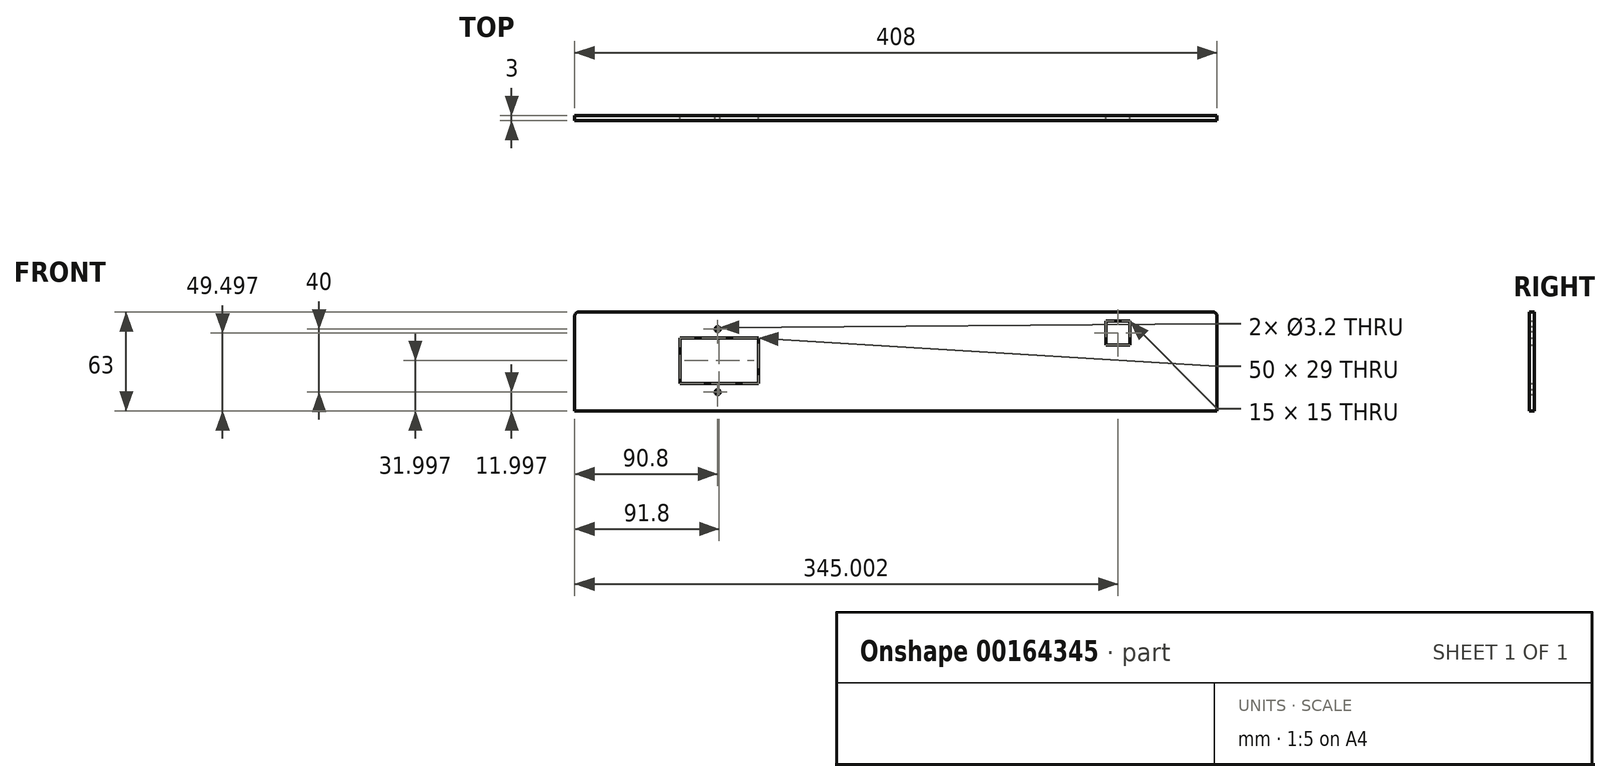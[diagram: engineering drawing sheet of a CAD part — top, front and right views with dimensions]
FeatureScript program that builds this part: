
annotation { "Feature Type Name" : "Feature", "Feature Type Description" : "" }
export const myFeature = defineFeature(function(context is Context, id is Id, definition is map)
    precondition{}
    {
        {
            var Q0;
            Q0=qCreatedBy(makeId("Front.planeOp"),FACE);
            var sketch = newSketch(context, id + "F0", { "sketchPlane" : qUnion([Q0])});
            skLineSegment(sketch, "E0.bottom", {"start": v(-225.79, -50.9) * mm, "end": v(176.21, -50.9) * mm});
            skLineSegment(sketch, "E0.top", {"start": v(-228.79, -113.9) * mm, "end": v(179.21, -113.9) * mm});
            skLineSegment(sketch, "E0.left", {"start": v(-228.79, -53.9) * mm, "end": v(-228.79, -113.9) * mm});
            skLineSegment(sketch, "E0.right", {"start": v(179.21, -53.9) * mm, "end": v(179.21, -113.9) * mm});
            skLineSegment(sketch, "E1.bottom", {"start": v(-162, -67.4) * mm, "end": v(-112, -67.4) * mm});
            skLineSegment(sketch, "E1.top", {"start": v(-162, -96.4) * mm, "end": v(-112, -96.4) * mm});
            skLineSegment(sketch, "E1.left", {"start": v(-162, -67.4) * mm, "end": v(-162, -96.4) * mm});
            skLineSegment(sketch, "E1.right", {"start": v(-112, -67.4) * mm, "end": v(-112, -96.4) * mm});
            skCircle(sketch, "E2", {"center": v(-138, -61.9) * mm, "radius": 1.6 * mm});
            skPoint(sketch, "E2.centerSnap0", {"position": v(-137, -67.4) * mm});
            skCircle(sketch, "E3", {"center": v(-138, -101.9) * mm, "radius": 1.6 * mm});
            skPoint(sketch, "E3.centerSnap0", {"position": v(-137, -96.4) * mm});
            skLineSegment(sketch, "E4.bottom", {"start": v(108.71, -56.9) * mm, "end": v(123.71, -56.9) * mm});
            skLineSegment(sketch, "E4.top", {"start": v(108.71, -71.9) * mm, "end": v(123.71, -71.9) * mm});
            skLineSegment(sketch, "E4.left", {"start": v(108.71, -56.9) * mm, "end": v(108.71, -71.9) * mm});
            skLineSegment(sketch, "E4.right", {"start": v(123.71, -56.9) * mm, "end": v(123.71, -71.9) * mm});
            skPoint(sketch, "E5.visualSharp", {"position": v(-228.79, -50.9) * mm});
            skArc(sketch, "E5.filletArc", {"start": v(-225.79, -50.9) * mm, "mid": v(-227.9, -51.77) * mm, "end": v(-228.79, -53.9) * mm});
            skPoint(sketch, "E6.visualSharp", {"position": v(179.21, -50.9) * mm});
            skArc(sketch, "E6.filletArc", {"start": v(179.21, -53.9) * mm, "mid": v(178.33, -51.77) * mm, "end": v(176.21, -50.9) * mm});
            skPoint(sketch, "E7.centerSnap0", {"position": v(179.21, -83.9) * mm});
            skLineSegment(sketch, "E8", {"start": v(-162, -81.9) * mm, "end": v(-112, -81.9) * mm, "construction": true});
            skSolve(sketch);
        }
        {
            var Q0;
            Q0 = qSketchRegion(id + "F0", true);
            extrude(context, id + "F1", {"entities" : qUnion([Q0]), "depth" : 3 * mm});
        }
    });
